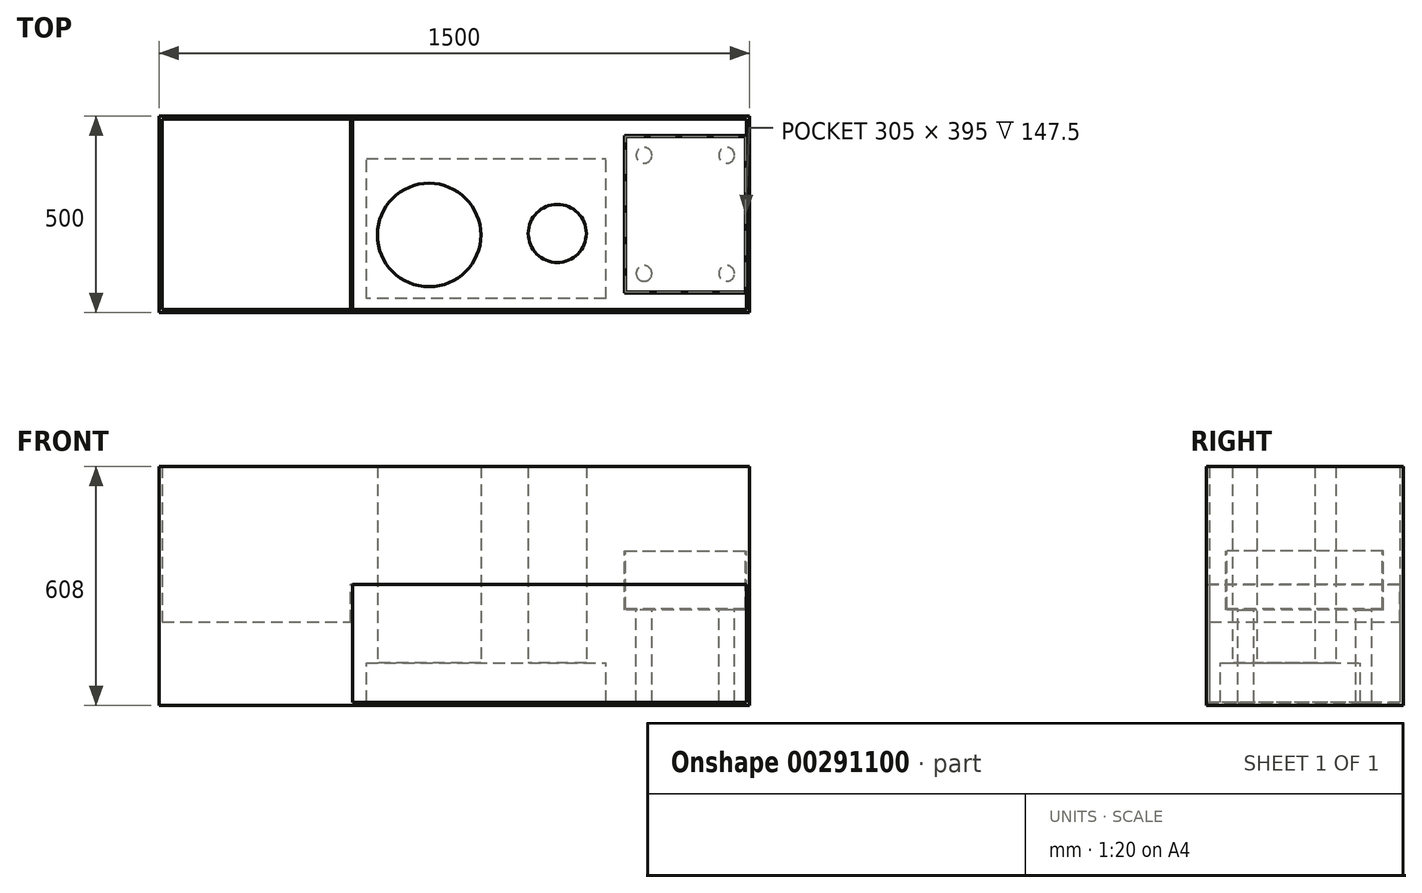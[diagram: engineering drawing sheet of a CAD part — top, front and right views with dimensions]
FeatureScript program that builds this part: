
annotation { "Feature Type Name" : "Feature", "Feature Type Description" : "" }
export const myFeature = defineFeature(function(context is Context, id is Id, definition is map)
    precondition{}
    {
        {
            var Q0;
            Q0=qCreatedBy(makeId("Top.planeOp"),FACE);
            var sketch = newSketch(context, id + "F0", { "sketchPlane" : qUnion([Q0])});
            skLineSegment(sketch, "E0.bottom", {"start": v(-750, 250) * mm, "end": v(750, 250) * mm});
            skLineSegment(sketch, "E0.top", {"start": v(-750, -250) * mm, "end": v(750, -250) * mm});
            skLineSegment(sketch, "E0.left", {"start": v(-750, 250) * mm, "end": v(-750, -250) * mm});
            skLineSegment(sketch, "E0.right", {"start": v(750, 250) * mm, "end": v(750, -250) * mm});
            skPoint(sketch, "E0.middle", {"position": v(0, 0) * mm});
            skLineSegment(sketch, "E1.bottom", {"start": v(-742, 242) * mm, "end": v(742, 242) * mm});
            skLineSegment(sketch, "E1.top", {"start": v(-742, -242) * mm, "end": v(742, -242) * mm});
            skLineSegment(sketch, "E1.left", {"start": v(-742, 242) * mm, "end": v(-742, -242) * mm});
            skLineSegment(sketch, "E1.right", {"start": v(742, 242) * mm, "end": v(742, -242) * mm});
            skSolve(sketch);
        }
        {
            var Q0;
            Q0=qSketchRegion(id+"F0",true);
            var Q1;
            Q1=makeQuery(id+"F0.imprint","IMPRINT",FACE,{"disambiguationData":[TD([[makeQuery(id+"F0.imprint","IMPRINT",EDGE,{"derivedFrom":sQuery(id+"F0.wireOp",EDGE,"E1.bottom")}),-1.0]])]});
            extrude(context, id + "F1", {"entities" : qUnion([Q0, Q1]), "oppositeDirection" : true, "depth" : 8 * mm});
        }
        {
            var Q0;
            Q0=qSketchRegion(id+"F0",true);
            extrude(context, id + "F2", {"entities" : qUnion([Q0]), "depth" : 600 * mm});
        }
        {
            var Q0;
            Q0=makeQuery(id+"F1.opExtrude","SWEPT_BODY",BODY,{"disambiguationData":[OSD([sQuery(id+"F0.wireOp",EDGE,"E0.bottom"),sQuery(id+"F0.wireOp",EDGE,"E0.top"),sQuery(id+"F0.wireOp",EDGE,"E0.left"),sQuery(id+"F0.wireOp",EDGE,"E0.right")])]});
            var Q1;
            Q1=makeQuery(id+"F2.opExtrude","SWEPT_BODY",BODY,{"disambiguationData":[OSD([sQuery(id+"F0.wireOp",EDGE,"E0.bottom"),sQuery(id+"F0.wireOp",EDGE,"E0.top"),sQuery(id+"F0.wireOp",EDGE,"E0.left"),sQuery(id+"F0.wireOp",EDGE,"E0.right"),sQuery(id+"F0.wireOp",EDGE,"E1.bottom"),sQuery(id+"F0.wireOp",EDGE,"E1.top"),sQuery(id+"F0.wireOp",EDGE,"E1.left"),sQuery(id+"F0.wireOp",EDGE,"E1.right")])]});
            booleanBodies(context, id + "F3", {"operationType" : BooleanOperationType.UNION, "tools" : qUnion([Q0, Q1])});
        }
        {
            var Q0;
            {var subQ0=sQuery(id+"F0.wireOp",EDGE,"E0.top");Q0=makeQuery(id+"F3.opBoolean","MERGE",FACE,{"derivedFrom":[makeQuery(id+"F1.opExtrude","SWEPT_FACE",FACE,{"disambiguationData":[OSD([subQ0])]}),makeQuery(id+"F2.opExtrude","SWEPT_FACE",FACE,{"disambiguationData":[OSD([subQ0])]})]});}
            var sketch = newSketch(context, id + "F4", { "sketchPlane" : qUnion([Q0])});
            skLineSegment(sketch, "E2", {"start": v(0, 0) * mm, "end": v(0, 341.46) * mm, "construction": true});
            skLineSegment(sketch, "E3.bottom", {"start": v(-258, 0) * mm, "end": v(-263, 0) * mm});
            skLineSegment(sketch, "E3.top", {"start": v(-258, 300) * mm, "end": v(-263, 300) * mm});
            skLineSegment(sketch, "E3.left", {"start": v(-258, 0) * mm, "end": v(-258, 300) * mm});
            skLineSegment(sketch, "E3.right", {"start": v(-263, 0) * mm, "end": v(-263, 300) * mm});
            skSolve(sketch);
        }
        {
            var Q0;
            Q0=qSketchRegion(id+"F4",true);
            var Q1;
            Q1=makeQuery(id+"F2.opExtrude","SWEPT_FACE",FACE,{"disambiguationData":[OSD([sQuery(id+"F0.wireOp",EDGE,"E1.bottom")])]});
            extrude(context, id + "F5", {"entities" : qUnion([Q0]), "endBound" : BoundingType.UP_TO_SURFACE, "oppositeDirection" : true, "endBoundEntityFace" : qUnion([Q1]), "depth" : 25 * mm});
        }
        {
            var Q0;
            Q0=qCreatedBy(makeId("Front.planeOp"),FACE);
            var sketch = newSketch(context, id + "F6", { "sketchPlane" : qUnion([Q0])});
            skLineSegment(sketch, "E4.0", {"start": v(472, 235) * mm, "end": v(432, 235) * mm});
            skLineSegment(sketch, "E5.0", {"start": v(742, 235) * mm, "end": v(702, 235) * mm});
            skLineSegment(sketch, "E6.bottom", {"start": v(432, 235) * mm, "end": v(742, 235) * mm});
            skLineSegment(sketch, "E6.top", {"start": v(432, 385) * mm, "end": v(742, 385) * mm});
            skLineSegment(sketch, "E6.left", {"start": v(432, 235) * mm, "end": v(432, 385) * mm});
            skLineSegment(sketch, "E6.right", {"start": v(742, 235) * mm, "end": v(742, 385) * mm});
            skSolve(sketch);
        }
        {
            var Q0;
            Q0=qSketchRegion(id+"F6",true);
            extrude(context, id + "F7", {"entities" : qUnion([Q0]), "oppositeDirection" : true, "depth" : 200 * mm, "hasSecondDirection" : true, "secondDirectionOppositeDirection" : false, "secondDirectionDepth" : 200 * mm});
        }
        {
            var Q0;
            Q0=makeQuery(id+"F7.opExtrude","SWEPT_FACE",FACE,{"disambiguationData":[OSD([sQuery(id+"F6.wireOp",EDGE,"E6.top")])]});
            shell(context, id + "F8", {"entities" : qUnion([Q0]), "thickness" : 2.5 * mm});
        }
        {
            var Q0;
            Q0=makeQuery(id+"F1.opExtrude","CAP_FACE",FACE,{"disambiguationData":[OSD([sQuery(id+"F0.wireOp",EDGE,"E0.bottom"),sQuery(id+"F0.wireOp",EDGE,"E0.top"),sQuery(id+"F0.wireOp",EDGE,"E0.left"),sQuery(id+"F0.wireOp",EDGE,"E0.right")])],"isStart":true});
            cPlane(context, id + "F9", {"entities" : qUnion([Q0]), "cplaneType" : CPlaneType.OFFSET, "offset" : 100 * mm, "width" : 150 * mm, "height" : 150 * mm});
        }
        {
            var Q0;
            Q0=qCreatedBy(id+"F9.planeOp",FACE);
            var sketch = newSketch(context, id + "F10", { "sketchPlane" : qUnion([Q0])});
            skCircle(sketch, "E7", {"center": v(-64.04, -52.45) * mm, "radius": 131.48 * mm});
            skCircle(sketch, "E8", {"center": v(261.6, -48.37) * mm, "radius": 73.85 * mm});
            skSolve(sketch);
        }
        {
            var Q0;
            Q0=qSketchRegion(id+"F10",true);
            extrude(context, id + "F11", {"entities" : qUnion([Q0]), "depth" : 500 * mm});
        }
        {
            var Q0;
            Q0=makeQuery(id+"F1.opExtrude","CAP_FACE",FACE,{"disambiguationData":[OSD([sQuery(id+"F0.wireOp",EDGE,"E0.bottom"),sQuery(id+"F0.wireOp",EDGE,"E0.top"),sQuery(id+"F0.wireOp",EDGE,"E0.left"),sQuery(id+"F0.wireOp",EDGE,"E0.right")])],"isStart":true});
            var sketch = newSketch(context, id + "F12", { "sketchPlane" : qUnion([Q0])});
            skLineSegment(sketch, "E9.bottom", {"start": v(-673.05, 170) * mm, "end": v(-479.58, 170) * mm});
            skLineSegment(sketch, "E9.top", {"start": v(-673.05, 63.71) * mm, "end": v(-479.58, 63.71) * mm});
            skLineSegment(sketch, "E9.left", {"start": v(-673.05, 170) * mm, "end": v(-673.05, 63.71) * mm});
            skLineSegment(sketch, "E9.right", {"start": v(-479.58, 170) * mm, "end": v(-479.58, 63.71) * mm});
            skSolve(sketch);
        }
        {
            var Q0;
            Q0=qSketchRegion(id+"F12",true);
            extrude(context, id + "F13", {"entities" : qUnion([Q0]), "depth" : 100 * mm});
        }
        {
            var Q0;
            Q0=makeQuery(id+"F7.opExtrude","SWEPT_FACE",FACE,{"disambiguationData":[OSD([sQuery(id+"F6.wireOp",EDGE,"E6.bottom")])]});
            var sketch = newSketch(context, id + "F14", { "sketchPlane" : qUnion([Q0])});
            skCircle(sketch, "E10", {"center": v(482, 150) * mm, "radius": 20 * mm});
            skLineSegment(sketch, "E11", {"start": v(587, 200) * mm, "end": v(587, -200) * mm, "construction": true});
            skLineSegment(sketch, "E12", {"start": v(432, 0) * mm, "end": v(742, 0) * mm, "construction": true});
            skCircle(sketch, "E13.MirrorC", {"center": v(692, 150) * mm, "radius": 20 * mm});
            skLineSegment(sketch, "E14.MirrorCS", {"start": v(742, 0) * mm, "end": v(432, 0) * mm, "construction": true});
            skCircle(sketch, "E15.MirrorC", {"center": v(692, -150) * mm, "radius": 20 * mm});
            skCircle(sketch, "E16.MirrorC", {"center": v(482, -150) * mm, "radius": 20 * mm});
            skSolve(sketch);
        }
        {
            var Q0;
            Q0=qSketchRegion(id+"F14",true);
            var Q1;
            Q1=makeQuery(id+"F1.opExtrude","CAP_FACE",FACE,{"disambiguationData":[OSD([sQuery(id+"F0.wireOp",EDGE,"E0.bottom"),sQuery(id+"F0.wireOp",EDGE,"E0.top"),sQuery(id+"F0.wireOp",EDGE,"E0.left"),sQuery(id+"F0.wireOp",EDGE,"E0.right")])],"isStart":false});
            extrude(context, id + "F15", {"entities" : qUnion([Q0]), "operationType" : NewBodyOperationType.ADD, "endBound" : BoundingType.UP_TO_SURFACE, "endBoundEntityFace" : qUnion([Q1]), "depth" : 25 * mm});
        }
        {
            var Q0;
            Q0=qCreatedBy(makeId("Front.planeOp"),FACE);
            var sketch = newSketch(context, id + "F16", { "sketchPlane" : qUnion([Q0])});
            skLineSegment(sketch, "E17.0", {"start": v(-258, 0) * mm, "end": v(-258, 300) * mm});
            skLineSegment(sketch, "E18.0", {"start": v(742, 600) * mm, "end": v(742, 0) * mm});
            skLineSegment(sketch, "E19.bottom", {"start": v(-258, 300) * mm, "end": v(742, 300) * mm});
            skLineSegment(sketch, "E19.top", {"start": v(-258, 0) * mm, "end": v(742, 0) * mm});
            skLineSegment(sketch, "E19.left", {"start": v(-258, 300) * mm, "end": v(-258, 0) * mm});
            skLineSegment(sketch, "E19.right", {"start": v(742, 300) * mm, "end": v(742, 0) * mm});
            skLineSegment(sketch, "E20.0", {"start": v(-263, 0) * mm, "end": v(-263, 300) * mm});
            skLineSegment(sketch, "E21.0", {"start": v(-742, 600) * mm, "end": v(-742, 0) * mm});
            skLineSegment(sketch, "E22.bottom", {"start": v(-263, 204.81) * mm, "end": v(-742, 204.81) * mm});
            skLineSegment(sketch, "E22.top", {"start": v(-263, 0) * mm, "end": v(-742, 0) * mm});
            skLineSegment(sketch, "E22.left", {"start": v(-263, 204.81) * mm, "end": v(-263, 0) * mm});
            skLineSegment(sketch, "E22.right", {"start": v(-742, 204.81) * mm, "end": v(-742, 0) * mm});
            skSolve(sketch);
        }
        {
            var Q0;
            Q0=makeQuery(id+"F16.imprint","IMPRINT",FACE,{"disambiguationData":[TD([[makeQuery(id+"F16.imprint","IMPRINT",EDGE,{"derivedFrom":sQuery(id+"F16.wireOp",EDGE,"E19.bottom")}),-1.0]])]});
            var Q1;
            Q1=makeQuery(id+"F16.imprint","IMPRINT",FACE,{"disambiguationData":[TD([[makeQuery(id+"F16.imprint","IMPRINT",EDGE,{"derivedFrom":sQuery(id+"F16.wireOp",EDGE,"E22.bottom")}),1.0]])]});
            var Q2;
            {var subQ0=sQuery(id+"F0.wireOp",EDGE,"E0.top");Q2=makeQuery(id+"F3.opBoolean","MERGE",FACE,{"derivedFrom":[makeQuery(id+"F1.opExtrude","SWEPT_FACE",FACE,{"disambiguationData":[OSD([subQ0])]}),makeQuery(id+"F2.opExtrude","SWEPT_FACE",FACE,{"disambiguationData":[OSD([subQ0])]})]});}
            var Q3;
            Q3=makeQuery(id+"F2.opExtrude","SWEPT_FACE",FACE,{"disambiguationData":[OSD([sQuery(id+"F0.wireOp",EDGE,"E1.bottom")])]});
            extrude(context, id + "F17", {"entities" : qUnion([Q0, Q1]), "endBound" : BoundingType.UP_TO_SURFACE, "endBoundEntityFace" : qUnion([Q2]), "depth" : 25 * mm, "hasSecondDirection" : true, "secondDirectionBound" : SecondDirectionBoundingType.UP_TO_SURFACE, "secondDirectionOppositeDirection" : true, "secondDirectionBoundEntityFace" : qUnion([Q3]), "secondDirectionDepth" : 25 * mm});
        }
        {
            var Q0;
            Q0=qCreatedBy(id+"F9.planeOp",FACE);
            var sketch = newSketch(context, id + "F18", { "sketchPlane" : qUnion([Q0])});
            skLineSegment(sketch, "E23.bottom", {"start": v(-223.35, -214.46) * mm, "end": v(385.43, -214.46) * mm});
            skLineSegment(sketch, "E23.top", {"start": v(-223.35, 141.33) * mm, "end": v(385.43, 141.33) * mm});
            skLineSegment(sketch, "E23.left", {"start": v(-223.35, -214.46) * mm, "end": v(-223.35, 141.33) * mm});
            skLineSegment(sketch, "E23.right", {"start": v(385.43, -214.46) * mm, "end": v(385.43, 141.33) * mm});
            skSolve(sketch);
        }
        {
            var Q0;
            Q0=makeQuery(id+"F18.imprint","IMPRINT",FACE,{"disambiguationData":[TD([[makeQuery(id+"F18.imprint","IMPRINT",EDGE,{"derivedFrom":sQuery(id+"F18.wireOp",EDGE,"E23.bottom")}),1.0]])]});
            extrude(context, id + "F19", {"entities" : qUnion([Q0]), "endBound" : BoundingType.UP_TO_NEXT, "oppositeDirection" : true, "depth" : 25 * mm});
        }
        {
            var Q0;
            Q0=makeQuery(id+"F16.imprint","IMPRINT",FACE,{"disambiguationData":[TD([[makeQuery(id+"F16.imprint","IMPRINT",EDGE,{"derivedFrom":sQuery(id+"F16.wireOp",EDGE,"E22.bottom")}),1.0]])]});
            extrude(context, id + "F20", {"entities" : qUnion([Q0]), "operationType" : NewBodyOperationType.ADD, "endBound" : BoundingType.UP_TO_NEXT, "oppositeDirection" : true, "depth" : 25 * mm, "hasSecondDirection" : true, "secondDirectionBound" : SecondDirectionBoundingType.UP_TO_NEXT, "secondDirectionOppositeDirection" : false, "secondDirectionDepth" : 25 * mm});
        }
    });
